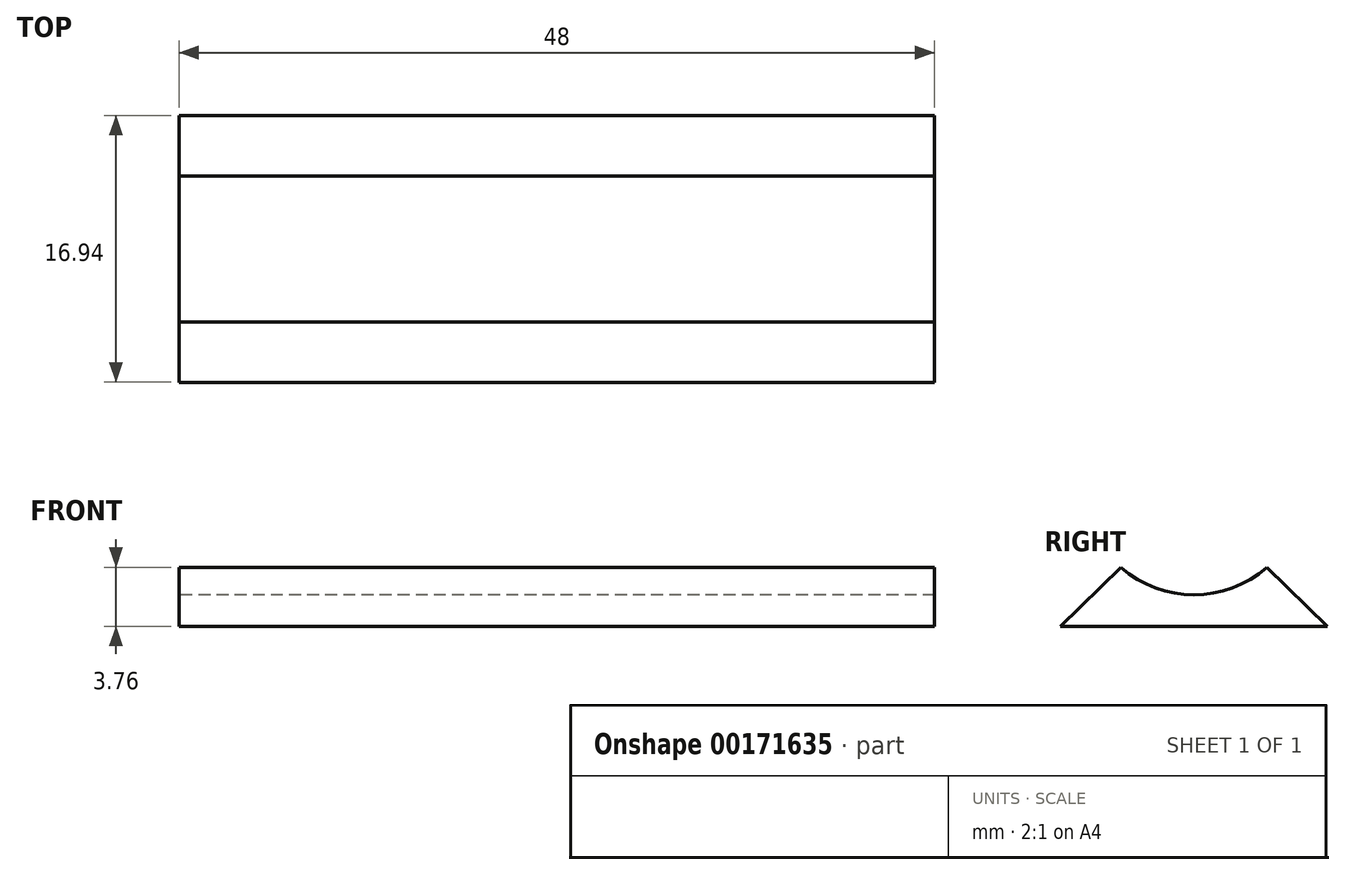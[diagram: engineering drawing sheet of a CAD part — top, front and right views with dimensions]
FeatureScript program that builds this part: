
annotation { "Feature Type Name" : "Feature", "Feature Type Description" : "" }
export const myFeature = defineFeature(function(context is Context, id is Id, definition is map)
    precondition{}
    {
        {
            var Q0;
            Q0=qCreatedBy(makeId("Right.planeOp"),FACE);
            var sketch = newSketch(context, id + "F0", { "sketchPlane" : qUnion([Q0])});
            skLineSegment(sketch, "E0", {"start": v(17.4, 0) * mm, "end": v(17.4, 9) * mm, "construction": true});
            skLineSegment(sketch, "E1", {"start": v(8.94, 0) * mm, "end": v(25.88, 0) * mm});
            skArc(sketch, "E2", {"start": v(12.77, 3.76) * mm, "mid": v(17.4, 2) * mm, "end": v(22.04, 3.76) * mm});
            skLineSegment(sketch, "E3", {"start": v(8.94, 0) * mm, "end": v(12.77, 3.76) * mm});
            skLineSegment(sketch, "E4", {"start": v(25.88, 0) * mm, "end": v(22.04, 3.76) * mm});
            skSolve(sketch);
        }
        {
            var Q0;
            Q0=makeQuery(id+"F0.imprint","IMPRINT",FACE,{"disambiguationData":[TD([[makeQuery(id+"F0.imprint","IMPRINT",EDGE,{"derivedFrom":sQuery(id+"F0.wireOp",EDGE,"E1")}),1.0]])]});
            extrude(context, id + "F1", {"entities" : qUnion([Q0]), "depth" : 48 * mm});
        }
    });
